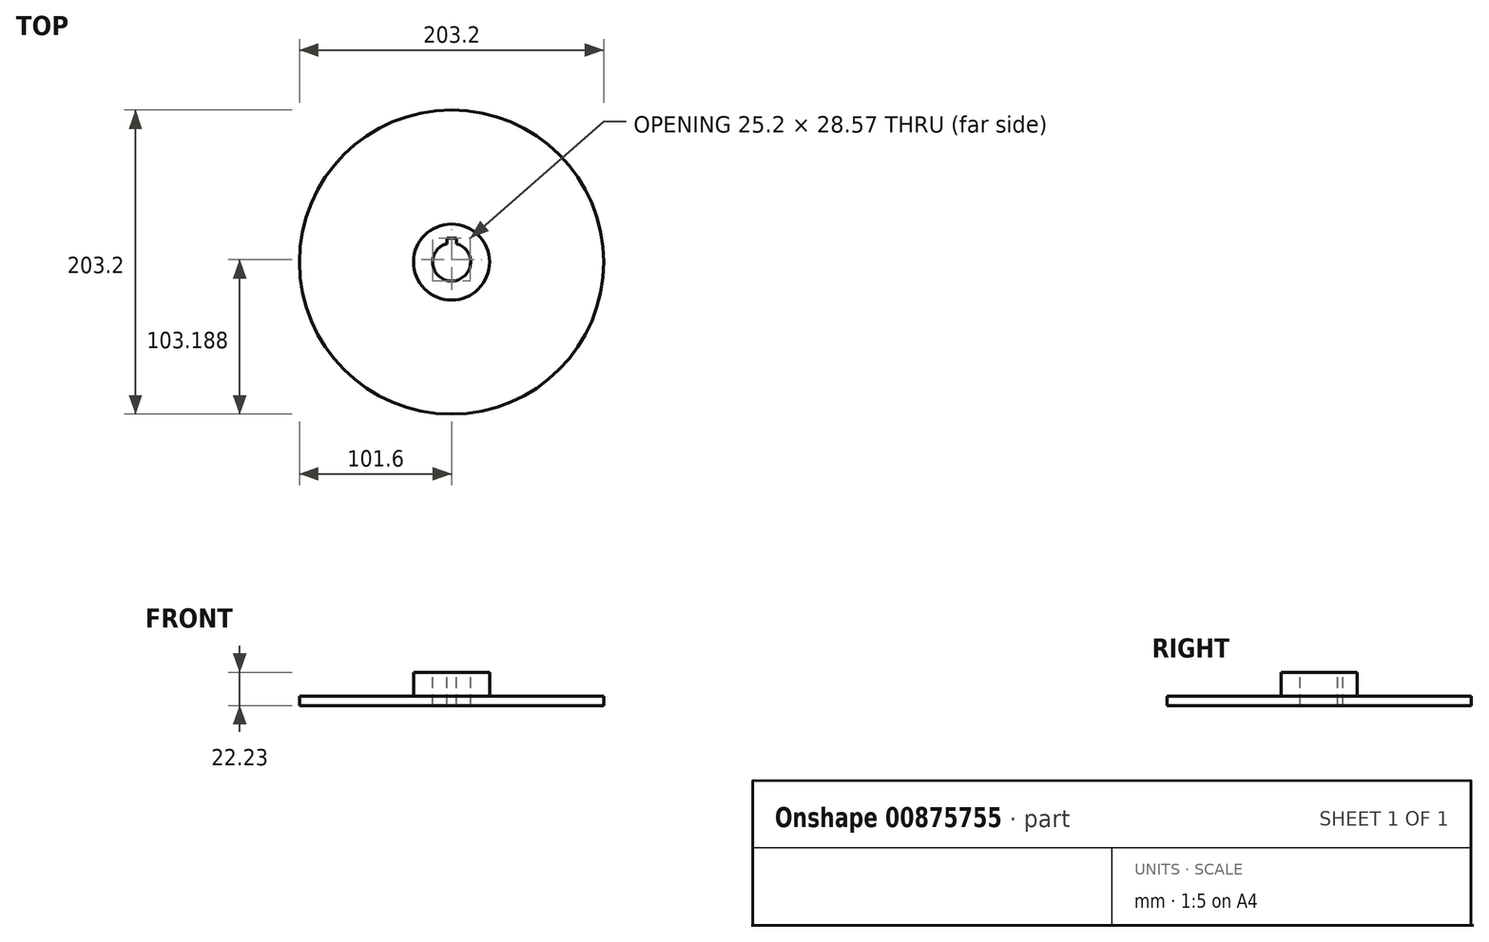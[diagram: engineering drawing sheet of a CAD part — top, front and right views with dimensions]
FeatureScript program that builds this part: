
annotation { "Feature Type Name" : "Feature", "Feature Type Description" : "" }
export const myFeature = defineFeature(function(context is Context, id is Id, definition is map)
    precondition{}
    {
        {
            var Q0;
            Q0=qCreatedBy(makeId("Top.planeOp"),FACE);
            var sketch = newSketch(context, id + "F0", { "sketchPlane" : qUnion([Q0])});
            skCircle(sketch, "E0", {"center": v(0, 0) * mm, "radius": 101.6 * mm});
            skSolve(sketch);
        }
        {
            var Q0;
            Q0 = qSketchRegion(id + "F0", true);
            extrude(context, id + "F1", {"entities" : qUnion([Q0]), "depth" : 6.35 * mm, "offsetDistance" : 25.4 * mm});
        }
        {
            var Q0;
            Q0=makeQuery(id+"F1.opExtrude","CAP_FACE",FACE,{"disambiguationData":[OSD([sQuery(id+"F0.wireOp",EDGE,"E0")])],"isStart":false});
            var sketch = newSketch(context, id + "F2", { "sketchPlane" : qUnion([Q0])});
            skCircle(sketch, "E1", {"center": v(0, 0) * mm, "radius": 25.4 * mm});
            skSolve(sketch);
        }
        {
            var Q0;
            Q0=makeQuery(id+"F2.imprint","IMPRINT",FACE,{"disambiguationData":[TD([[makeQuery(id+"F2.imprint","IMPRINT",EDGE,{"derivedFrom":sQuery(id+"F2.wireOp",EDGE,"E1")}),1.0]])]});
            extrude(context, id + "F3", {"entities" : qUnion([Q0]), "operationType" : NewBodyOperationType.ADD, "depth" : 15.88 * mm, "offsetDistance" : 25.4 * mm});
        }
        {
            var Q0;
            Q0=makeQuery(id+"F3.opExtrude","CAP_FACE",FACE,{"disambiguationData":[OSD([sQuery(id+"F2.wireOp",EDGE,"E1")])],"isStart":false});
            var sketch = newSketch(context, id + "F4", { "sketchPlane" : qUnion([Q0])});
            skCircle(sketch, "E2", {"center": v(0, 0) * mm, "radius": 12.7 * mm});
            skLineSegment(sketch, "E3.bottom", {"start": v(3.17, 15.88) * mm, "end": v(-3.18, 15.88) * mm});
            skLineSegment(sketch, "E3.top", {"start": v(3.17, 9.53) * mm, "end": v(-3.18, 9.53) * mm});
            skLineSegment(sketch, "E3.left", {"start": v(3.17, 15.88) * mm, "end": v(3.17, 9.53) * mm});
            skLineSegment(sketch, "E3.right", {"start": v(-3.18, 15.88) * mm, "end": v(-3.18, 9.53) * mm});
            skPoint(sketch, "E3.middle", {"position": v(0, 12.7) * mm});
            skSolve(sketch);
        }
        {
            var Q0;
            {var subQ5=sQuery(id+"F4.wireOp",EDGE,"E3.top");Q0=makeQuery(id+"F4.imprint","IMPRINT",FACE,{"disambiguationData":[TD([[makeQuery(id+"F4.imprint","IMPRINT",EDGE,{"derivedFrom":subQ5}),1.0]])]});}
            var Q1;
            {var subQ5=sQuery(id+"F4.wireOp",EDGE,"E3.top");Q1=makeQuery(id+"F4.imprint","IMPRINT",FACE,{"disambiguationData":[TD([[makeQuery(id+"F4.imprint","IMPRINT",EDGE,{"derivedFrom":subQ5}),-1.0]])]});}
            var Q2;
            {var subQ5=sQuery(id+"F4.wireOp",EDGE,"E3.bottom");Q2=makeQuery(id+"F4.imprint","IMPRINT",FACE,{"disambiguationData":[TD([[makeQuery(id+"F4.imprint","IMPRINT",EDGE,{"derivedFrom":subQ5}),1.0]])]});}
            extrude(context, id + "F5", {"entities" : qUnion([Q0, Q1, Q2]), "operationType" : NewBodyOperationType.REMOVE, "endBound" : BoundingType.THROUGH_ALL, "oppositeDirection" : true, "depth" : 25.4 * mm, "offsetDistance" : 25.4 * mm});
        }
    });
